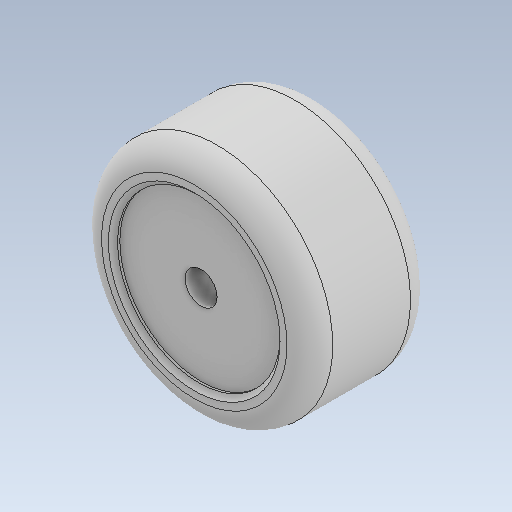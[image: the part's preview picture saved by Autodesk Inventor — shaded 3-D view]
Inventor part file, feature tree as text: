
AUTODESK INVENTOR PART (.ipt)
format: ipt  version: 2021.3 (Build 253353000, 353)  size: 177,152 bytes
history: native  units: mm
features: extrude x3, sketch x1, chamfer x1, fillet x1
ambient origin geometry x8: Origin, YZ Plane, XZ Plane, XY Plane, X Axis, Y Axis, Z Axis, Center Point
bodies: Solid1 (feature_tree)
feature tree (6):
  sketch  "Sketch2"  dims[d0=101.0mm d1=3.0mm d2=15.0mm d3=14.0mm d4=27.0mm d5=27.0mm d6=0.0mm d7=0.0mm d8=3.0mm d9=0.0mm d10=3.0mm d11=0.0mm d12=2.0mm d13=2.0mm d14=45.0deg d15=10.0mm]
  extrude  "Extrusion1"  Depth=3.0mm
  extrude  "Extrusion2"  Depth=10.0mm
  extrude  "Extrusion3"  Depth=10.0mm
  chamfer  "Chamfer1"  Distance=27.0mm
  fillet  "Fillet1"  Radius=3.0mm
